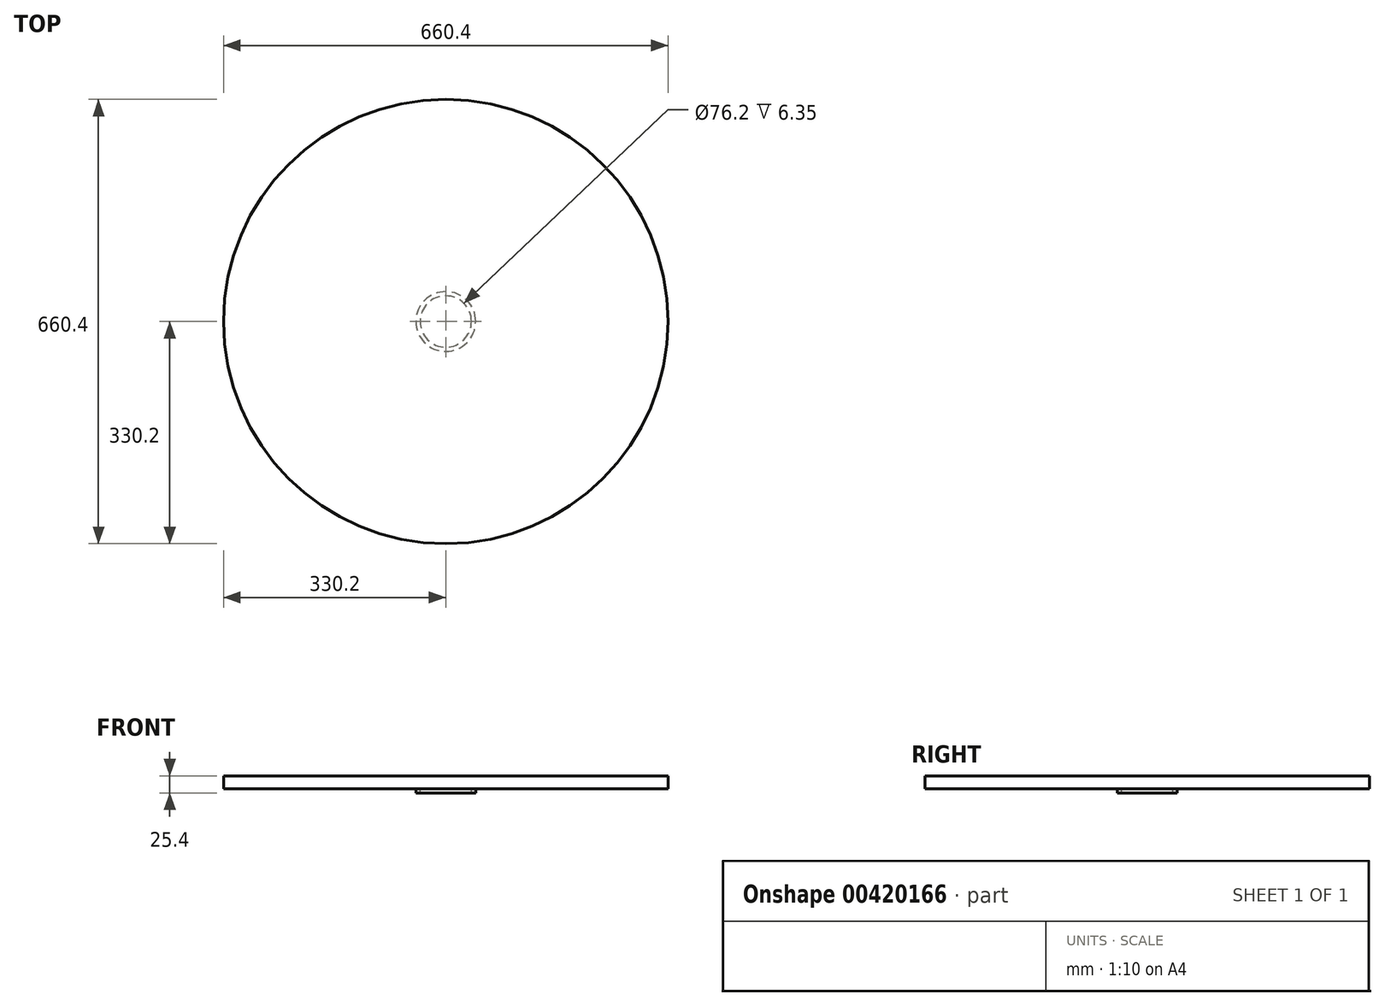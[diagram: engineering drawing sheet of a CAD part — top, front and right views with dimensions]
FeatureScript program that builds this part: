
annotation { "Feature Type Name" : "Feature", "Feature Type Description" : "" }
export const myFeature = defineFeature(function(context is Context, id is Id, definition is map)
    precondition{}
    {
        {
            var Q0;
            Q0=qCreatedBy(makeId("Top.planeOp"),FACE);
            var sketch = newSketch(context, id + "F0", { "sketchPlane" : qUnion([Q0])});
            skCircle(sketch, "E0", {"center": v(0, 0) * mm, "radius": 330.2 * mm});
            skSolve(sketch);
        }
        {
            var Q0;
            Q0=makeQuery(id+"F0.imprint","IMPRINT",FACE,{"disambiguationData":[TD([[makeQuery(id+"F0.imprint","IMPRINT",EDGE,{"derivedFrom":sQuery(id+"F0.wireOp",EDGE,"E0")}),1.0]])]});
            var Q1;
            Q1=sQuery(id+"F0.wireOp",EDGE,"E0");
            extrude(context, id + "F1", {"entities" : qUnion([Q0]), "surfaceEntities" : qUnion([Q1]), "depth" : 19.05 * mm});
        }
        {
            var Q0;
            Q0=qCreatedBy(makeId("Top.planeOp"),FACE);
            var sketch = newSketch(context, id + "F2", { "sketchPlane" : qUnion([Q0])});
            skLineSegment(sketch, "E1.bottom", {"start": v(-44.45, -44.45) * mm, "end": v(44.45, -44.45) * mm});
            skLineSegment(sketch, "E1.top", {"start": v(-44.45, 44.45) * mm, "end": v(44.45, 44.45) * mm});
            skLineSegment(sketch, "E1.left", {"start": v(-44.45, -44.45) * mm, "end": v(-44.45, 44.45) * mm});
            skLineSegment(sketch, "E1.right", {"start": v(44.45, -44.45) * mm, "end": v(44.45, 44.45) * mm});
            skPoint(sketch, "E2", {"position": v(0, -44.45) * mm});
            skPoint(sketch, "E3", {"position": v(-44.45, 0) * mm});
            skCircle(sketch, "E4", {"center": v(0, 0) * mm, "radius": 44.45 * mm});
            skCircle(sketch, "E5", {"center": v(0, 0) * mm, "radius": 38.1 * mm});
            skSolve(sketch);
        }
        {
            var Q0;
            Q0=makeQuery(id+"F2.imprint","IMPRINT",FACE,{"disambiguationData":[TD([[makeQuery(id+"F2.imprint","IMPRINT",EDGE,{"derivedFrom":sQuery(id+"F2.wireOp",EDGE,"E5")}),-1.0]])]});
            extrude(context, id + "F3", {"entities" : qUnion([Q0]), "operationType" : NewBodyOperationType.ADD, "oppositeDirection" : true, "depth" : 6.35 * mm});
        }
    });
